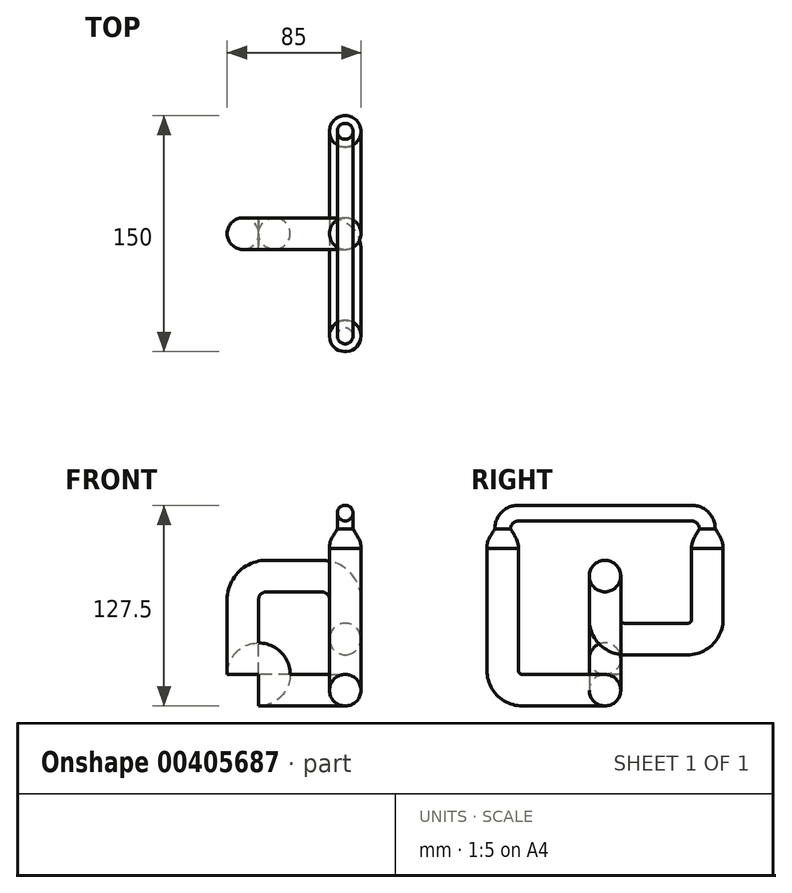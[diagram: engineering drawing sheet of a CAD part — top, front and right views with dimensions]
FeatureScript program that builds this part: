
annotation { "Feature Type Name" : "Feature", "Feature Type Description" : "" }
export const myFeature = defineFeature(function(context is Context, id is Id, definition is map)
    precondition{}
    {
        {
            var Q0;
            Q0=qCreatedBy(makeId("Top.planeOp"),FACE);
            var sketch = newSketch(context, id + "F0", { "sketchPlane" : qUnion([Q0])});
            skCircle(sketch, "E0", {"center": v(0, 0) * mm, "radius": 10 * mm});
            skLineSegment(sketch, "E1", {"start": v(0, 0) * mm, "end": v(65, 0) * mm});
            skPoint(sketch, "E2", {"position": v(65, 12.5) * mm});
            skSolve(sketch);
        }
        {
            var Q0;
            Q0=qCreatedBy(makeId("Right.planeOp"),FACE);
            var sketch = newSketch(context, id + "F1", { "sketchPlane" : qUnion([Q0])});
            skLineSegment(sketch, "E3.0", {"start": v(-10, 0) * mm, "end": v(10, 0) * mm});
            skSolve(sketch);
        }
        {
            var Q0;
            Q0=qCreatedBy(makeId("Front.planeOp"),FACE);
            var sketch = newSketch(context, id + "F2", { "sketchPlane" : qUnion([Q0])});
            skArc(sketch, "E4.0", {"start": v(15, 40) * mm, "mid": v(4.4, 35.6) * mm, "end": v(0, 25) * mm});
            skLineSegment(sketch, "E5.0", {"start": v(45, 40) * mm, "end": v(15, 40) * mm});
            skLineSegment(sketch, "E5.1", {"start": v(50, 40) * mm, "end": v(45, 40) * mm});
            skArc(sketch, "E5.2", {"start": v(50, 40) * mm, "mid": v(60.6, 35.6) * mm, "end": v(65, 25) * mm});
            skLineSegment(sketch, "E5.3", {"start": v(65, 25) * mm, "end": v(65, 12.5) * mm});
            skPoint(sketch, "E6", {"position": v(65, 12.5) * mm});
            skPoint(sketch, "E7.orphan", {"position": v(65, 0) * mm});
            skArc(sketch, "E8", {"start": v(0, -22.5) * mm, "mid": v(2.93, -29.57) * mm, "end": v(10, -32.5) * mm});
            skPoint(sketch, "E9", {"position": v(0, 0) * mm});
            skLineSegment(sketch, "E10", {"start": v(0, 25) * mm, "end": v(0, 0) * mm});
            skLineSegment(sketch, "E11", {"start": v(0, 0) * mm, "end": v(0, -22.5) * mm});
            skSolve(sketch);
        }
        {
            var Q0;
            Q0=makeQuery(id+"F0.imprint","IMPRINT",FACE,{"disambiguationData":[TD([[makeQuery(id+"F0.imprint","IMPRINT",EDGE,{"derivedFrom":sQuery(id+"F0.wireOp",EDGE,"E0")}),1.0]])]});
            var Q1;
            Q1=sQuery(id+"F2.wireOp",EDGE,"E10");
            var Q2;
            Q2=sQuery(id+"F2.wireOp",EDGE,"E4.0");
            var Q3;
            Q3=sQuery(id+"F2.wireOp",EDGE,"E5.0");
            var Q4;
            Q4=sQuery(id+"F2.wireOp",EDGE,"E5.1");
            var Q5;
            Q5=sQuery(id+"F2.wireOp",EDGE,"E5.2");
            var Q6;
            Q6=sQuery(id+"F2.wireOp",EDGE,"E5.3");
            sweep(context, id + "F3", {"profiles" : qUnion([Q0]), "path" : qUnion([Q1, Q2, Q3, Q4, Q5, Q6])});
        }
        {
            var Q0;
            Q0=qCreatedBy(makeId("Right.planeOp"),FACE);
            var Q1;
            Q1=qBodyType(qCreatedBy(id+"F5",EDGE),BodyType.WIRE);
            cPlane(context, id + "F4", {"entities" : qUnion([Q0, Q1]), "cplaneType" : CPlaneType.OFFSET, "offset" : 65 * mm, "width" : 150 * mm, "height" : 150 * mm});
        }
        {
            var Q0;
            Q0=qCreatedBy(id+"F4.planeOp",FACE);
            var sketch = newSketch(context, id + "F5", { "sketchPlane" : qUnion([Q0])});
            skPoint(sketch, "E12.0", {"position": v(0, 12.5) * mm});
            skPoint(sketch, "E13.0", {"position": v(12.5, 0) * mm});
            skArc(sketch, "E14", {"start": v(12.5, 0) * mm, "mid": v(3.66, 3.66) * mm, "end": v(0, 12.5) * mm});
            skLineSegment(sketch, "E15", {"start": v(12.5, 0) * mm, "end": v(52.5, 0) * mm});
            skArc(sketch, "E16", {"start": v(52.5, 0) * mm, "mid": v(61.34, 3.66) * mm, "end": v(65, 12.5) * mm});
            skLineSegment(sketch, "E17", {"start": v(65, 12.5) * mm, "end": v(65, 57.5) * mm});
            skLineSegment(sketch, "E18", {"start": v(65, 0) * mm, "end": v(65, 70) * mm});
            skPoint(sketch, "E18.endSnap0", {"position": v(65, 35) * mm});
            skArc(sketch, "E19", {"start": v(65, 70) * mm, "mid": v(62.07, 77.07) * mm, "end": v(55, 80) * mm});
            skLineSegment(sketch, "E20", {"start": v(55, 80) * mm, "end": v(-35, 80) * mm});
            skLineSegment(sketch, "E21", {"start": v(-35, 80) * mm, "end": v(-55, 80) * mm});
            skArc(sketch, "E22", {"start": v(-55, 80) * mm, "mid": v(-62.07, 77.07) * mm, "end": v(-65, 70) * mm});
            skLineSegment(sketch, "E23", {"start": v(-65, 0) * mm, "end": v(-65, 57.5) * mm});
            skLineSegment(sketch, "E24", {"start": v(-65, 0) * mm, "end": v(-65, -20) * mm});
            skArc(sketch, "E25", {"start": v(-65, -20) * mm, "mid": v(-61.34, -28.84) * mm, "end": v(-52.5, -32.5) * mm});
            skPoint(sketch, "E26.0", {"position": v(-10, 0) * mm});
            skLineSegment(sketch, "E27", {"start": v(-10, -32.5) * mm, "end": v(-52.5, -32.5) * mm});
            skSolve(sketch);
        }
        {
            var Q0;
            Q0=qCreatedBy(makeId("Front.planeOp"),FACE);
            cPlane(context, id + "F6", {"entities" : qUnion([Q0]), "cplaneType" : CPlaneType.OFFSET, "offset" : 52.5 * mm, "oppositeDirection" : true, "width" : 150 * mm, "height" : 150 * mm});
        }
        {
            var Q0;
            Q0=qCreatedBy(id+"F6.planeOp",FACE);
            var sketch = newSketch(context, id + "F7", { "sketchPlane" : qUnion([Q0])});
            skPoint(sketch, "E28.0", {"position": v(65, 0) * mm});
            skCircle(sketch, "E29", {"center": v(65, 0) * mm, "radius": 10 * mm});
            skSolve(sketch);
        }
        {
            var Q0;
            Q0=makeQuery(id+"F7.imprint","IMPRINT",FACE,{"disambiguationData":[TD([[makeQuery(id+"F7.imprint","IMPRINT",EDGE,{"derivedFrom":sQuery(id+"F7.wireOp",EDGE,"E29")}),1.0]])]});
            var Q1;
            Q1=sQuery(id+"F5.wireOp",EDGE,"E15");
            var Q2;
            Q2=sQuery(id+"F5.wireOp",EDGE,"E14");
            sweep(context, id + "F8", {"operationType" : NewBodyOperationType.ADD, "profiles" : qUnion([Q0]), "path" : qUnion([Q1, Q2])});
        }
        {
            var Q0;
            Q0=makeQuery(id+"F8.opSweep","CAP_FACE",FACE,{"disambiguationData":[OSD([sQuery(id+"F5.wireOp",VERTEX,"E15.end"),sQuery(id+"F7.wireOp",EDGE,"E29")])],"isStart":true});
            var Q1;
            Q1=sQuery(id+"F5.wireOp",EDGE,"E16");
            var Q2;
            Q2=sQuery(id+"F5.wireOp",EDGE,"E17");
            sweep(context, id + "F9", {"operationType" : NewBodyOperationType.ADD, "profiles" : qUnion([Q0]), "path" : qUnion([Q1, Q2])});
        }
        {
            var Q0;
            Q0=qCreatedBy(makeId("Top.planeOp"),FACE);
            cPlane(context, id + "F10", {"entities" : qUnion([Q0]), "cplaneType" : CPlaneType.OFFSET, "offset" : 70 * mm, "width" : 150 * mm, "height" : 150 * mm});
        }
        {
            var Q0;
            Q0=qCreatedBy(id+"F10.planeOp",FACE);
            var sketch = newSketch(context, id + "F11", { "sketchPlane" : qUnion([Q0])});
            skPoint(sketch, "E30.0", {"position": v(65, 65) * mm});
            skCircle(sketch, "E31", {"center": v(65, 65) * mm, "radius": 5 * mm});
            skSolve(sketch);
        }
        {
            var Q0;
            Q0=makeQuery(id+"F11.imprint","IMPRINT",FACE,{"disambiguationData":[TD([[makeQuery(id+"F11.imprint","IMPRINT",EDGE,{"derivedFrom":sQuery(id+"F11.wireOp",EDGE,"E31")}),1.0]])]});
            var Q1;
            Q1=sQuery(id+"F5.wireOp",EDGE,"E19");
            var Q2;
            Q2=sQuery(id+"F5.wireOp",EDGE,"E20");
            var Q3;
            Q3=sQuery(id+"F5.wireOp",EDGE,"E21");
            var Q4;
            Q4=sQuery(id+"F5.wireOp",EDGE,"E22");
            sweep(context, id + "F12", {"profiles" : qUnion([Q0]), "path" : qUnion([Q1, Q2, Q3, Q4])});
        }
        {
            var Q0;
            Q0=makeQuery(id+"F9.opSweep","CAP_FACE",FACE,{"disambiguationData":[OSD([sQuery(id+"F5.wireOp",VERTEX,"E15.end"),sQuery(id+"F5.wireOp",VERTEX,"E17.end"),sQuery(id+"F7.wireOp",EDGE,"E29")])],"isStart":false});
            var Q1;
            Q1=makeQuery(id+"F12.opSweep","CAP_FACE",FACE,{"disambiguationData":[OSD([sQuery(id+"F5.wireOp",VERTEX,"E19.start"),sQuery(id+"F11.wireOp",EDGE,"E31")])],"isStart":true});
            loft(context, id + "F13", {"startCondition" : LoftEndDerivativeType.MATCH_CURVATURE, "startMagnitude" : 1, "endCondition" : LoftEndDerivativeType.MATCH_CURVATURE, "endMagnitude" : 0, "sheetProfilesArray" : [{ "sheetProfileEntities" : qUnion([Q0]) }, { "sheetProfileEntities" : qUnion([Q1]) }]});
        }
        {
            var Q0;
            Q0=qCreatedBy(makeId("Front.planeOp"),FACE);
            cPlane(context, id + "F14", {"entities" : qUnion([Q0]), "cplaneType" : CPlaneType.OFFSET, "offset" : 10 * mm, "width" : 150 * mm, "height" : 150 * mm});
        }
        {
            var Q0;
            Q0=qCreatedBy(id+"F14.planeOp",FACE);
            var sketch = newSketch(context, id + "F15", { "sketchPlane" : qUnion([Q0])});
            skPoint(sketch, "E32.0", {"position": v(65, -32.5) * mm});
            skCircle(sketch, "E33", {"center": v(65, -32.5) * mm, "radius": 10 * mm});
            skSolve(sketch);
        }
        {
            var Q0;
            Q0=makeQuery(id+"F15.imprint","IMPRINT",FACE,{"disambiguationData":[TD([[makeQuery(id+"F15.imprint","IMPRINT",EDGE,{"derivedFrom":sQuery(id+"F15.wireOp",EDGE,"E33")}),1.0]])]});
            var Q1;
            Q1=sQuery(id+"F5.wireOp",EDGE,"E27");
            var Q2;
            Q2=sQuery(id+"F5.wireOp",EDGE,"E25");
            var Q3;
            Q3=sQuery(id+"F5.wireOp",EDGE,"E24");
            var Q4;
            Q4=sQuery(id+"F5.wireOp",EDGE,"E23");
            sweep(context, id + "F16", {"profiles" : qUnion([Q0]), "path" : qUnion([Q1, Q2, Q3, Q4])});
        }
        {
            var Q0;
            Q0=makeQuery(id+"F12.opSweep","CAP_FACE",FACE,{"disambiguationData":[OSD([sQuery(id+"F5.wireOp",VERTEX,"E22.end"),sQuery(id+"F11.wireOp",EDGE,"E31")])],"isStart":false});
            var Q1;
            Q1=makeQuery(id+"F16.opSweep","CAP_FACE",FACE,{"disambiguationData":[OSD([sQuery(id+"F5.wireOp",VERTEX,"E23.end"),sQuery(id+"F15.wireOp",EDGE,"E33")])],"isStart":false});
            loft(context, id + "F17", {"startCondition" : LoftEndDerivativeType.MATCH_CURVATURE, "startMagnitude" : 0, "endCondition" : LoftEndDerivativeType.MATCH_CURVATURE, "endMagnitude" : 1, "sheetProfilesArray" : [{ "sheetProfileEntities" : qUnion([Q0]) }, { "sheetProfileEntities" : qUnion([Q1]) }]});
        }
        {
            var Q0;
            Q0=qCreatedBy(makeId("Top.planeOp"),FACE);
            cPlane(context, id + "F18", {"entities" : qUnion([Q0]), "cplaneType" : CPlaneType.OFFSET, "offset" : 32.5 * mm, "oppositeDirection" : true, "width" : 150 * mm, "height" : 150 * mm});
        }
        {
            var Q0;
            Q0=qCreatedBy(id+"F18.planeOp",FACE);
            var sketch = newSketch(context, id + "F19", { "sketchPlane" : qUnion([Q0])});
            skPoint(sketch, "E34.0", {"position": v(65, -10) * mm});
            skPoint(sketch, "E35.0", {"position": v(65, 0) * mm});
            skArc(sketch, "E36", {"start": v(65, -10) * mm, "mid": v(62.07, -2.93) * mm, "end": v(55, 0) * mm});
            skLineSegment(sketch, "E37.0", {"start": v(15, 0) * mm, "end": v(0, 0) * mm});
            skCircle(sketch, "E38.0", {"center": v(0, 0) * mm, "radius": 10 * mm});
            skLineSegment(sketch, "E39", {"start": v(55, 0) * mm, "end": v(10, 0) * mm});
            skSolve(sketch);
        }
        {
            var Q0;
            Q0=makeQuery(id+"F15.imprint","IMPRINT",FACE,{"disambiguationData":[TD([[makeQuery(id+"F15.imprint","IMPRINT",EDGE,{"derivedFrom":sQuery(id+"F15.wireOp",EDGE,"E33")}),1.0]])]});
            var Q1;
            Q1=sQuery(id+"F19.wireOp",EDGE,"E36");
            var Q2;
            Q2=sQuery(id+"F19.wireOp",EDGE,"E39");
            sweep(context, id + "F20", {"operationType" : NewBodyOperationType.ADD, "profiles" : qUnion([Q0]), "path" : qUnion([Q1, Q2])});
        }
        {
            var Q0;
            Q0=makeQuery(id+"F0.imprint","IMPRINT",FACE,{"disambiguationData":[TD([[makeQuery(id+"F0.imprint","IMPRINT",EDGE,{"derivedFrom":sQuery(id+"F0.wireOp",EDGE,"E0")}),1.0]])]});
            var Q1;
            Q1=sQuery(id+"F2.wireOp",EDGE,"E11");
            var Q2;
            Q2=sQuery(id+"F2.wireOp",EDGE,"E8");
            sweep(context, id + "F21", {"operationType" : NewBodyOperationType.ADD, "profiles" : qUnion([Q0]), "path" : qUnion([Q1, Q2])});
        }
    });
